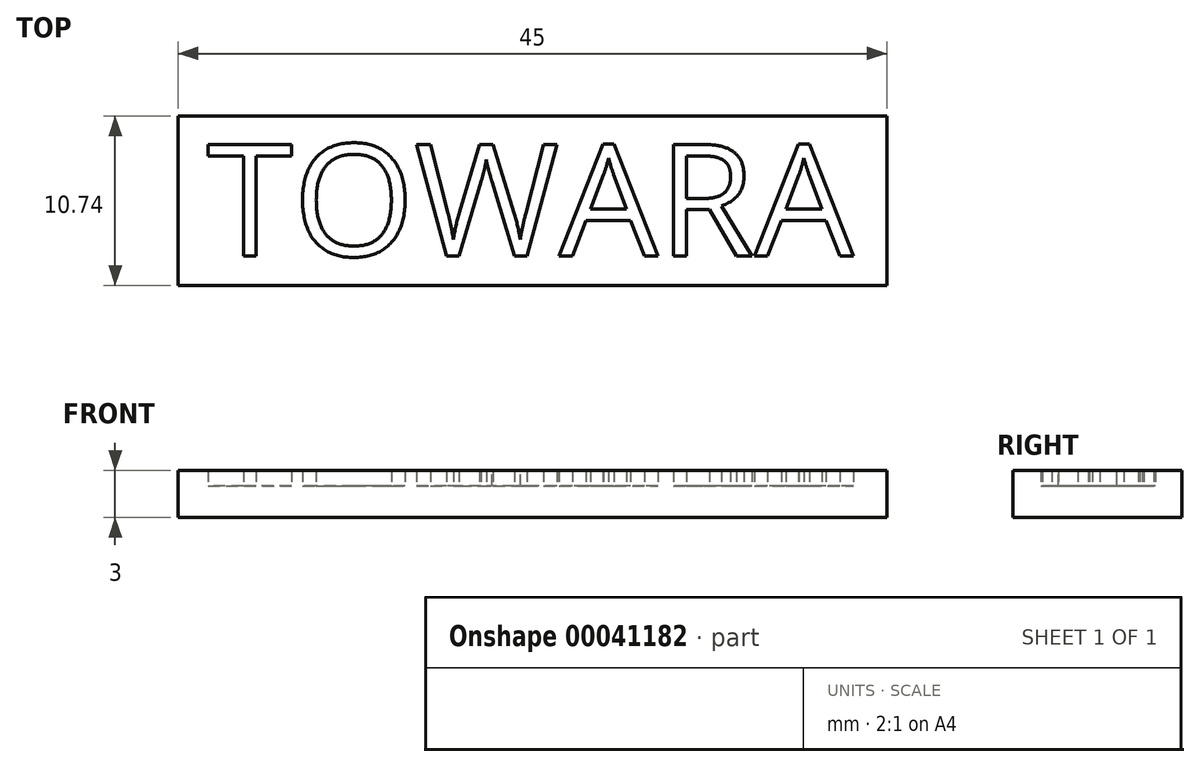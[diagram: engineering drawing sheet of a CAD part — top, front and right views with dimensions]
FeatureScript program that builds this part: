
annotation { "Feature Type Name" : "Feature", "Feature Type Description" : "" }
export const myFeature = defineFeature(function(context is Context, id is Id, definition is map)
    precondition{}
    {
        {
            var Q0;
            Q0=qCreatedBy(makeId("Top.planeOp"),FACE);
            var sketch = newSketch(context, id + "F0", { "sketchPlane" : qUnion([Q0])});
            skText(sketch, "E0", { "text": "TOWARA", "fontName": "OpenSans-Regular.ttf"});
            skLineSegment(sketch, "E1.bottom", {"start": v(-1.8, 1.73) * mm, "end": v(43.2, 1.73) * mm});
            skLineSegment(sketch, "E1.top", {"start": v(-1.8, -9) * mm, "end": v(43.2, -9) * mm});
            skLineSegment(sketch, "E1.left", {"start": v(-1.8, 1.73) * mm, "end": v(-1.8, -9) * mm});
            skLineSegment(sketch, "E1.right", {"start": v(43.2, 1.73) * mm, "end": v(43.2, -9) * mm});
            const initialGuessF0  = {"E0": [0, -0.00714, 1, 0, 0.00714]};
            skSetInitialGuess(sketch, initialGuessF0);
            skSolve(sketch);
        }
        {
            var Q0;
            Q0=qCreatedBy(makeId("Top.planeOp"),FACE);
            cPlane(context, id + "F1", {"entities" : qUnion([Q0]), "cplaneType" : CPlaneType.OFFSET, "offset" : 2 * mm, "oppositeDirection" : true, "width" : 150 * mm, "height" : 150 * mm});
        }
        {
            var Q0;
            Q0=qCreatedBy(id+"F1.planeOp",FACE);
            var sketch = newSketch(context, id + "F2", { "sketchPlane" : qUnion([Q0])});
            skLineSegment(sketch, "E2.0", {"start": v(-1.8, 1.73) * mm, "end": v(43.2, 1.73) * mm});
            skLineSegment(sketch, "E3.0", {"start": v(-1.8, 1.73) * mm, "end": v(-1.8, -9) * mm});
            skLineSegment(sketch, "E4.0", {"start": v(-1.8, -9) * mm, "end": v(43.2, -9) * mm});
            skLineSegment(sketch, "E5.0", {"start": v(43.2, 1.73) * mm, "end": v(43.2, -9) * mm});
            skSolve(sketch);
        }
        {
            var Q0;
            Q0=makeQuery(id+"F2.imprint","IMPRINT",FACE,{"disambiguationData":[TD([[makeQuery(id+"F2.imprint","IMPRINT",EDGE,{"derivedFrom":sQuery(id+"F2.wireOp",EDGE,"E2.0")}),-1.0]])]});
            extrude(context, id + "F3", {"entities" : qUnion([Q0]), "depth" : 2 * mm});
        }
        {
            var Q0;
            Q0=makeQuery(id+"F0.imprint","IMPRINT",FACE,{"disambiguationData":[TD([[makeQuery(id+"F0.imprint","IMPRINT",EDGE,{"derivedFrom":sQuery(id+"F0.wireOp",EDGE,"E0.sketch_text.stroke-0")}),1.0]])]});
            var Q1;
            Q1=makeQuery(id+"F0.imprint","IMPRINT",FACE,{"disambiguationData":[TD([[makeQuery(id+"F0.imprint","IMPRINT",EDGE,{"derivedFrom":sQuery(id+"F0.wireOp",EDGE,"E0.sketch_text.stroke-16")}),1.0]])]});
            var Q2;
            Q2=makeQuery(id+"F0.imprint","IMPRINT",FACE,{"disambiguationData":[TD([[makeQuery(id+"F0.imprint","IMPRINT",EDGE,{"derivedFrom":sQuery(id+"F0.wireOp",EDGE,"E0.sketch_text.stroke-52")}),1.0]])]});
            var Q3;
            Q3=makeQuery(id+"F0.imprint","IMPRINT",FACE,{"disambiguationData":[TD([[makeQuery(id+"F0.imprint","IMPRINT",EDGE,{"derivedFrom":sQuery(id+"F0.wireOp",EDGE,"E0.sketch_text.stroke-68")}),1.0]])]});
            var Q4;
            Q4=makeQuery(id+"F0.imprint","IMPRINT",FACE,{"disambiguationData":[TD([[makeQuery(id+"F0.imprint","IMPRINT",EDGE,{"derivedFrom":sQuery(id+"F0.wireOp",EDGE,"E0.sketch_text.stroke-83")}),1.0]])]});
            extrude(context, id + "F4", {"entities" : qUnion([Q0, Q1, Q2, Q3, Q4]), "operationType" : NewBodyOperationType.ADD, "depth" : 1 * mm});
        }
    });
